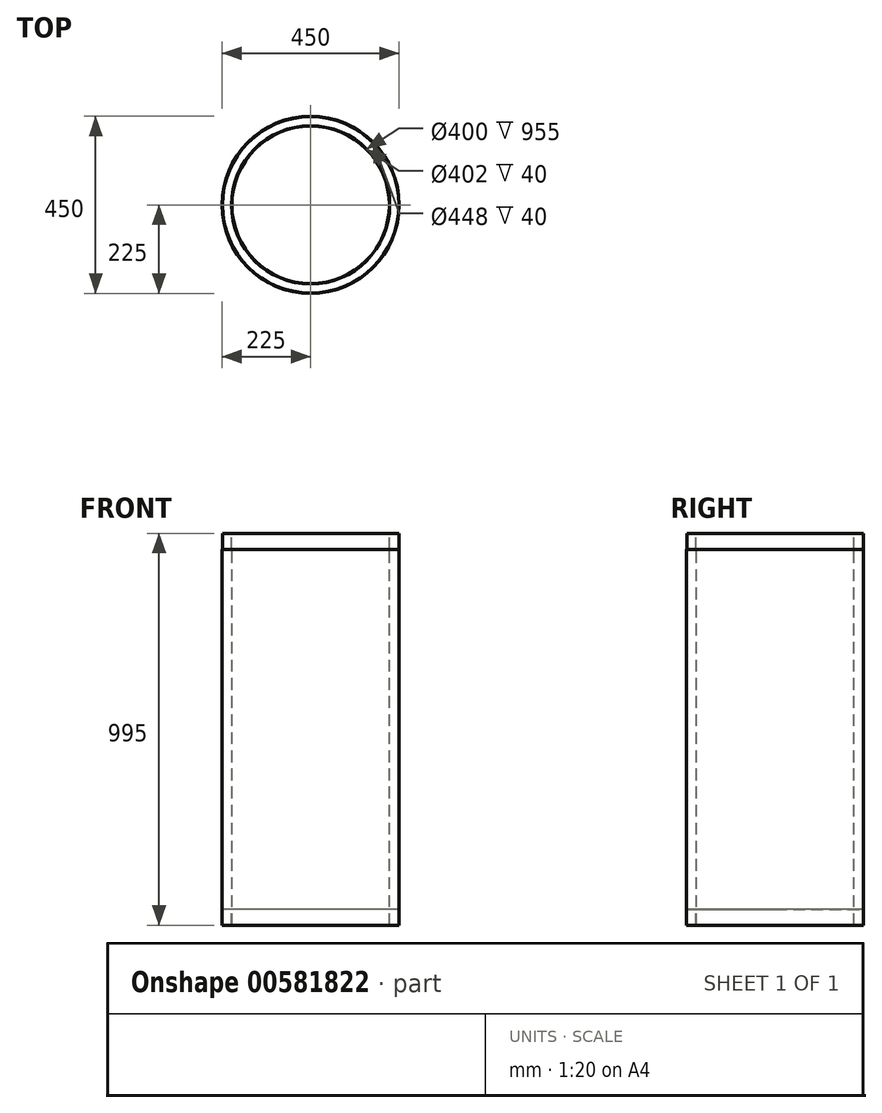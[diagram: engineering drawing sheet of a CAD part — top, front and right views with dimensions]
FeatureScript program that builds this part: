
annotation { "Feature Type Name" : "Feature", "Feature Type Description" : "" }
export const myFeature = defineFeature(function(context is Context, id is Id, definition is map)
    precondition{}
    {
        {
            var Q0;
            Q0=qCreatedBy(makeId("Front.planeOp"),FACE);
            var sketch = newSketch(context, id + "F0", { "sketchPlane" : qUnion([Q0])});
            skLineSegment(sketch, "E0", {"start": v(0, 345.75) * mm, "end": v(0, -558.03) * mm, "construction": true});
            skLineSegment(sketch, "E1", {"start": v(-200, -518.84) * mm, "end": v(-200, 436.16) * mm});
            skLineSegment(sketch, "E2", {"start": v(-200, 436.16) * mm, "end": v(-201, 436.16) * mm});
            skLineSegment(sketch, "E3", {"start": v(-201, 436.16) * mm, "end": v(-201, 476.16) * mm});
            skLineSegment(sketch, "E4", {"start": v(-201, 476.16) * mm, "end": v(-224, 476.16) * mm});
            skLineSegment(sketch, "E5", {"start": v(-224, 476.16) * mm, "end": v(-224, 436.16) * mm});
            skLineSegment(sketch, "E6", {"start": v(-224, 436.16) * mm, "end": v(-225, 436.16) * mm});
            skLineSegment(sketch, "E7", {"start": v(-225, 436.16) * mm, "end": v(-225, -518.84) * mm});
            skLineSegment(sketch, "E8", {"start": v(-225, -518.84) * mm, "end": v(-224, -518.84) * mm});
            skLineSegment(sketch, "E9", {"start": v(-224, -518.84) * mm, "end": v(-224, -478.84) * mm});
            skLineSegment(sketch, "E10", {"start": v(-224, -478.84) * mm, "end": v(-201, -478.84) * mm});
            skLineSegment(sketch, "E11", {"start": v(-201, -478.84) * mm, "end": v(-201, -518.84) * mm});
            skLineSegment(sketch, "E12", {"start": v(-201, -518.84) * mm, "end": v(-200, -518.84) * mm});
            skSolve(sketch);
        }
        {
            var Q0;
            Q0=qSketchRegion(id+"F0",true);
            var Q1;
            Q1=sQuery(id+"F0.wireOp",EDGE,"E0");
            revolve(context, id + "F1", {"entities" : qUnion([Q0]), "axis" : qUnion([Q1]), "revolveType" : RevolveType.FULL});
        }
    });
